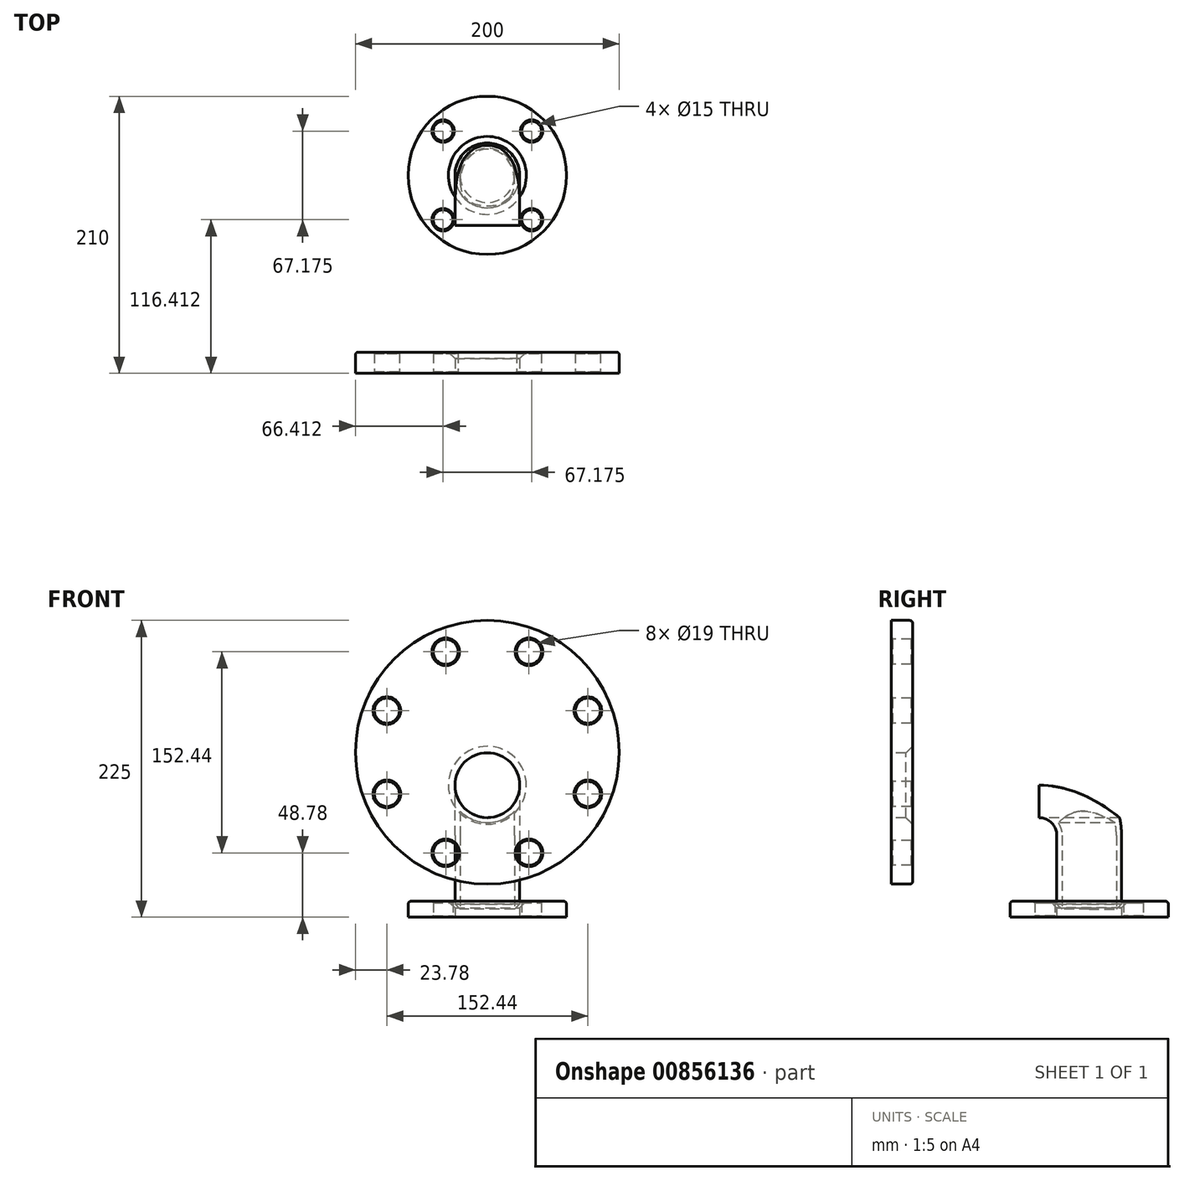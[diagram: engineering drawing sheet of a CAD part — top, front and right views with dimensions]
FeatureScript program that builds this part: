
annotation { "Feature Type Name" : "Feature", "Feature Type Description" : "" }
export const myFeature = defineFeature(function(context is Context, id is Id, definition is map)
    precondition{}
    {
        {
            var Q0;
            Q0=qCreatedBy(makeId("Front.planeOp"),FACE);
            var sketch = newSketch(context, id + "F0", { "sketchPlane" : qUnion([Q0])});
            skCircle(sketch, "E0", {"center": v(0, 0) * mm, "radius": 100 * mm});
            skCircle(sketch, "E1", {"center": v(0, 0) * mm, "radius": 82.5 * mm, "construction": true});
            skLineSegment(sketch, "E2", {"start": v(133.72, 0) * mm, "end": v(-112.74, 0) * mm, "construction": true});
            skLineSegment(sketch, "E3", {"start": v(0, 107.77) * mm, "end": v(0, -109.7) * mm, "construction": true});
            skLineSegment(sketch, "E4", {"start": v(0, 0) * mm, "end": v(85.32, 35.34) * mm, "construction": true});
            skCircle(sketch, "E5", {"center": v(76.22, 31.57) * mm, "radius": 9.5 * mm});
            skCircle(sketch, "E6.1.0", {"center": v(31.57, 76.22) * mm, "radius": 9.5 * mm});
            skCircle(sketch, "E6.2.0", {"center": v(-31.57, 76.22) * mm, "radius": 9.5 * mm});
            skCircle(sketch, "E6.3.0", {"center": v(-76.22, 31.57) * mm, "radius": 9.5 * mm});
            skCircle(sketch, "E6.4.0", {"center": v(-76.22, -31.57) * mm, "radius": 9.5 * mm});
            skCircle(sketch, "E6.5.0", {"center": v(-31.57, -76.22) * mm, "radius": 9.5 * mm});
            skCircle(sketch, "E6.6.0", {"center": v(31.57, -76.22) * mm, "radius": 9.5 * mm});
            skCircle(sketch, "E6.7.0", {"center": v(76.22, -31.57) * mm, "radius": 9.5 * mm});
            skSolve(sketch);
        }
        {
            var Q0;
            Q0=makeQuery(id+"F0.imprint","IMPRINT",FACE,{"disambiguationData":[TD([[makeQuery(id+"F0.imprint","IMPRINT",EDGE,{"derivedFrom":sQuery(id+"F0.wireOp",EDGE,"E0")}),1.0]])]});
            extrude(context, id + "F1", {"entities" : qUnion([Q0]), "oppositeDirection" : true, "depth" : 16 * mm, "offsetDistance" : 25 * mm});
        }
        {
            var Q0;
            Q0=makeQuery(id+"F1.opExtrude","CAP_EDGE",EDGE,{"disambiguationData":[OSD([sQuery(id+"F0.wireOp",EDGE,"E0")])],"isStart":false});
            fillet(context, id + "F2", {"entities" : qUnion([Q0]), "radius" : 2 * mm, "tangentPropagation" : true, "allowEdgeOverflow" : false});
        }
        {
            var Q0;
            Q0=qCreatedBy(makeId("Front.planeOp"),FACE);
            cPlane(context, id + "F3", {"entities" : qUnion([Q0]), "cplaneType" : CPlaneType.OFFSET, "offset" : 5 * mm, "oppositeDirection" : true, "width" : 150 * mm, "height" : 150 * mm});
        }
        {
            var Q0;
            Q0=qCreatedBy(id+"F3.planeOp",FACE);
            var sketch = newSketch(context, id + "F4", { "sketchPlane" : qUnion([Q0])});
            skLineSegment(sketch, "E7", {"start": v(82.9, 0) * mm, "end": v(-83.79, 0) * mm, "construction": true});
            skLineSegment(sketch, "E8", {"start": v(0, 79.6) * mm, "end": v(0, -86.48) * mm, "construction": true});
            skLineSegment(sketch, "E9.0", {"start": v(82.9, -25) * mm, "end": v(-83.79, -25) * mm, "construction": true});
            skCircle(sketch, "E10", {"center": v(0, -25) * mm, "radius": 24.55 * mm});
            skSolve(sketch);
        }
        {
            var Q0;
            Q0=qCreatedBy(makeId("Right.planeOp"),FACE);
            var sketch = newSketch(context, id + "F5", { "sketchPlane" : qUnion([Q0])});
            skLineSegment(sketch, "E11", {"start": v(-20.78, 0) * mm, "end": v(160.74, 0) * mm, "construction": true});
            skLineSegment(sketch, "E12", {"start": v(0, 92.54) * mm, "end": v(0, -98.93) * mm, "construction": true});
            skLineSegment(sketch, "E13.0", {"start": v(5, -25) * mm, "end": v(111.9, -25) * mm});
            skLineSegment(sketch, "E14.0", {"start": v(5, 92.54) * mm, "end": v(5, -98.93) * mm, "construction": true});
            skLineSegment(sketch, "E15.0", {"start": v(150, -63.1) * mm, "end": v(150, -120) * mm});
            skLineSegment(sketch, "E16.0", {"start": v(5, -120) * mm, "end": v(160.74, -120) * mm, "construction": true});
            skArc(sketch, "E17.filletArc", {"start": v(150, -63.1) * mm, "mid": v(138.84, -36.16) * mm, "end": v(111.9, -25) * mm});
            skSolve(sketch);
        }
        {
            var Q0;
            Q0=makeQuery(id+"F4.imprint","IMPRINT",FACE,{"disambiguationData":[TD([[makeQuery(id+"F4.imprint","IMPRINT",EDGE,{"derivedFrom":sQuery(id+"F4.wireOp",EDGE,"E10")}),1.0]])]});
            var Q1;
            Q1=sQuery(id+"F5.wireOp",EDGE,"E13.0");
            var Q2;
            Q2=sQuery(id+"F5.wireOp",EDGE,"E17.filletArc");
            var Q3;
            Q3=sQuery(id+"F5.wireOp",EDGE,"E15.0");
            sweep(context, id + "F6", {"profiles" : qUnion([Q0]), "path" : qUnion([Q1, Q2, Q3])});
        }
        {
            var Q0;
            Q0=makeQuery(id+"F1.opExtrude","CAP_FACE",FACE,{"disambiguationData":[OSD([sQuery(id+"F0.wireOp",EDGE,"E0"),sQuery(id+"F0.wireOp",EDGE,"E5"),sQuery(id+"F0.wireOp",EDGE,"E6.1.0"),sQuery(id+"F0.wireOp",EDGE,"E6.2.0"),sQuery(id+"F0.wireOp",EDGE,"E6.3.0"),sQuery(id+"F0.wireOp",EDGE,"E6.4.0"),sQuery(id+"F0.wireOp",EDGE,"E6.5.0"),sQuery(id+"F0.wireOp",EDGE,"E6.6.0"),sQuery(id+"F0.wireOp",EDGE,"E6.7.0")])],"isStart":true});
            var sketch = newSketch(context, id + "F7", { "sketchPlane" : qUnion([Q0])});
            skLineSegment(sketch, "E18", {"start": v(111.86, 0) * mm, "end": v(-112.16, 0) * mm, "construction": true});
            skLineSegment(sketch, "E19", {"start": v(0, 108.58) * mm, "end": v(0, -128) * mm, "construction": true});
            skLineSegment(sketch, "E20.0", {"start": v(111.86, -25) * mm, "end": v(-112.16, -25) * mm, "construction": true});
            skCircle(sketch, "E21", {"center": v(0, -25) * mm, "radius": 24.55 * mm});
            skSolve(sketch);
        }
        {
            var Q0;
            Q0=makeQuery(id+"F7.imprint","IMPRINT",FACE,{"disambiguationData":[TD([[makeQuery(id+"F7.imprint","IMPRINT",EDGE,{"derivedFrom":sQuery(id+"F7.wireOp",EDGE,"E21")}),1.0]])]});
            extrude(context, id + "F8", {"entities" : qUnion([Q0]), "operationType" : NewBodyOperationType.REMOVE, "endBound" : BoundingType.THROUGH_ALL, "oppositeDirection" : true, "depth" : 6 * mm, "offsetDistance" : 25 * mm});
        }
        {
            var Q0;
            Q0=makeQuery(id+"F6.opSweep","CAP_FACE",FACE,{"disambiguationData":[OSD([sQuery(id+"F4.wireOp",EDGE,"E10"),sQuery(id+"F5.wireOp",VERTEX,"E13.0.start")])],"isStart":true});
            var Q1;
            Q1=makeQuery(id+"F6.opSweep","CAP_FACE",FACE,{"disambiguationData":[OSD([sQuery(id+"F4.wireOp",EDGE,"E10"),sQuery(id+"F5.wireOp",VERTEX,"E15.0.end")])],"isStart":false});
            shell(context, id + "F9", {"entities" : qUnion([Q0, Q1]), "thickness" : 3.95 * mm});
        }
        {
            var Q0;
            Q0=makeQuery(id+"F6.opSweep","CAP_FACE",FACE,{"disambiguationData":[OSD([sQuery(id+"F4.wireOp",EDGE,"E10"),sQuery(id+"F5.wireOp",VERTEX,"E15.0.end")])],"isStart":false});
            cPlane(context, id + "F10", {"entities" : qUnion([Q0]), "cplaneType" : CPlaneType.OFFSET, "offset" : 5 * mm, "width" : 150 * mm, "height" : 150 * mm});
        }
        {
            var Q0;
            Q0=qCreatedBy(id+"F10.planeOp",FACE);
            var sketch = newSketch(context, id + "F11", { "sketchPlane" : qUnion([Q0])});
            skLineSegment(sketch, "E22", {"start": v(0, -213.4) * mm, "end": v(0, 8.6) * mm, "construction": true});
            skLineSegment(sketch, "E23", {"start": v(-108.24, 0) * mm, "end": v(105.98, 0) * mm, "construction": true});
            skLineSegment(sketch, "E24.0", {"start": v(-108.24, -150) * mm, "end": v(105.98, -150) * mm, "construction": true});
            skCircle(sketch, "E25", {"center": v(0, -150) * mm, "radius": 24.55 * mm});
            skCircle(sketch, "E26", {"center": v(0, -150) * mm, "radius": 47.5 * mm, "construction": true});
            skCircle(sketch, "E27", {"center": v(0, -150) * mm, "radius": 60 * mm});
            skLineSegment(sketch, "E28", {"start": v(0, -150) * mm, "end": v(49.53, -199.53) * mm, "construction": true});
            skCircle(sketch, "E29", {"center": v(33.59, -183.59) * mm, "radius": 7.5 * mm});
            skCircle(sketch, "E30.1.0", {"center": v(33.59, -116.41) * mm, "radius": 7.5 * mm});
            skCircle(sketch, "E30.2.0", {"center": v(-33.59, -116.41) * mm, "radius": 7.5 * mm});
            skCircle(sketch, "E30.3.0", {"center": v(-33.59, -183.59) * mm, "radius": 7.5 * mm});
            skSolve(sketch);
        }
        {
            var Q0;
            Q0=makeQuery(id+"F11.imprint","IMPRINT",FACE,{"disambiguationData":[TD([[makeQuery(id+"F11.imprint","IMPRINT",EDGE,{"derivedFrom":sQuery(id+"F11.wireOp",EDGE,"E25")}),-1.0]])]});
            extrude(context, id + "F12", {"entities" : qUnion([Q0]), "oppositeDirection" : true, "depth" : 12 * mm, "offsetDistance" : 25 * mm});
        }
        {
            var Q0;
            Q0=makeQuery(id+"F12.opExtrude","CAP_EDGE",EDGE,{"disambiguationData":[OSD([sQuery(id+"F11.wireOp",EDGE,"E27")])],"isStart":false});
            fillet(context, id + "F13", {"entities" : qUnion([Q0]), "radius" : 2 * mm, "tangentPropagation" : true, "allowEdgeOverflow" : false});
        }
        {
            var Q0;
            Q0=makeQuery(id+"F6.opSweep","CAP_EDGE",EDGE,{"disambiguationData":[OSD([sQuery(id+"F4.wireOp",EDGE,"E10"),sQuery(id+"F5.wireOp",VERTEX,"E13.0.start")])],"isStart":true});
            var Q1;
            Q1=makeQuery(id+"F6.opSweep","CAP_EDGE",EDGE,{"disambiguationData":[OSD([sQuery(id+"F4.wireOp",EDGE,"E10"),sQuery(id+"F5.wireOp",VERTEX,"E15.0.end")])],"isStart":false});
            var Q2;
            Q2=makeQuery(id+"F8.boolean.opBoolean","INTERSECT",EDGE,{"derivedFrom":[makeQuery(id+"F1.opExtrude","CAP_FACE",FACE,{"disambiguationData":[OSD([sQuery(id+"F0.wireOp",EDGE,"E0"),sQuery(id+"F0.wireOp",EDGE,"E5"),sQuery(id+"F0.wireOp",EDGE,"E6.1.0"),sQuery(id+"F0.wireOp",EDGE,"E6.2.0"),sQuery(id+"F0.wireOp",EDGE,"E6.3.0"),sQuery(id+"F0.wireOp",EDGE,"E6.4.0"),sQuery(id+"F0.wireOp",EDGE,"E6.5.0"),sQuery(id+"F0.wireOp",EDGE,"E6.6.0"),sQuery(id+"F0.wireOp",EDGE,"E6.7.0")])],"isStart":false}),makeQuery(id+"F8.opExtrude","SWEPT_FACE",FACE,{"disambiguationData":[OSD([sQuery(id+"F7.wireOp",EDGE,"E21")])]})]});
            var Q3;
            Q3=makeQuery(id+"F12.opExtrude","CAP_EDGE",EDGE,{"disambiguationData":[OSD([sQuery(id+"F11.wireOp",EDGE,"E25")])],"isStart":false});
            chamfer(context, id + "F14", {"entities" : qUnion([Q0, Q1, Q2, Q3]), "width" : 5 * mm, "tangentPropagation" : true});
        }
        {
            var Q0;
            Q0=makeQuery(id+"F1.opExtrude","SWEPT_FACE",FACE,{"disambiguationData":[OSD([sQuery(id+"F0.wireOp",EDGE,"E6.1.0")])]});
            var Q1;
            Q1=makeQuery(id+"F1.opExtrude","SWEPT_FACE",FACE,{"disambiguationData":[OSD([sQuery(id+"F0.wireOp",EDGE,"E6.2.0")])]});
            var Q2;
            Q2=makeQuery(id+"F1.opExtrude","SWEPT_FACE",FACE,{"disambiguationData":[OSD([sQuery(id+"F0.wireOp",EDGE,"E5")])]});
            var Q3;
            Q3=makeQuery(id+"F1.opExtrude","SWEPT_FACE",FACE,{"disambiguationData":[OSD([sQuery(id+"F0.wireOp",EDGE,"E6.7.0")])]});
            var Q4;
            Q4=makeQuery(id+"F1.opExtrude","SWEPT_FACE",FACE,{"disambiguationData":[OSD([sQuery(id+"F0.wireOp",EDGE,"E6.6.0")])]});
            var Q5;
            Q5=makeQuery(id+"F1.opExtrude","SWEPT_FACE",FACE,{"disambiguationData":[OSD([sQuery(id+"F0.wireOp",EDGE,"E6.5.0")])]});
            var Q6;
            Q6=makeQuery(id+"F1.opExtrude","SWEPT_FACE",FACE,{"disambiguationData":[OSD([sQuery(id+"F0.wireOp",EDGE,"E6.4.0")])]});
            var Q7;
            Q7=makeQuery(id+"F1.opExtrude","SWEPT_FACE",FACE,{"disambiguationData":[OSD([sQuery(id+"F0.wireOp",EDGE,"E6.3.0")])]});
            var Q8;
            Q8=makeQuery(id+"F12.opExtrude","SWEPT_FACE",FACE,{"disambiguationData":[OSD([sQuery(id+"F11.wireOp",EDGE,"E30.2.0")])]});
            var Q9;
            Q9=makeQuery(id+"F12.opExtrude","SWEPT_FACE",FACE,{"disambiguationData":[OSD([sQuery(id+"F11.wireOp",EDGE,"E30.3.0")])]});
            var Q10;
            Q10=makeQuery(id+"F12.opExtrude","SWEPT_FACE",FACE,{"disambiguationData":[OSD([sQuery(id+"F11.wireOp",EDGE,"E29")])]});
            var Q11;
            Q11=makeQuery(id+"F12.opExtrude","SWEPT_FACE",FACE,{"disambiguationData":[OSD([sQuery(id+"F11.wireOp",EDGE,"E30.1.0")])]});
            chamfer(context, id + "F15", {"entities" : qUnion([Q0, Q1, Q2, Q3, Q4, Q5, Q6, Q7, Q8, Q9, Q10, Q11]), "width" : 1 * mm, "tangentPropagation" : true});
        }
    });
